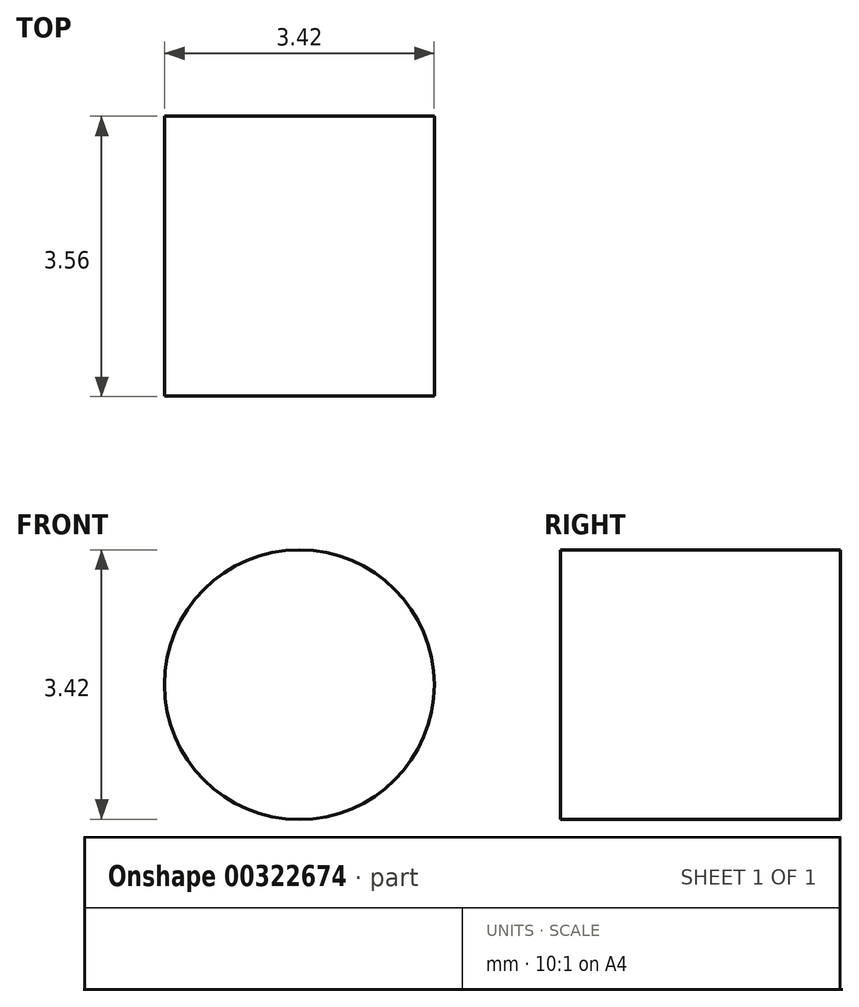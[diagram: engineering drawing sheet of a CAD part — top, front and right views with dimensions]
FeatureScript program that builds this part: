
annotation { "Feature Type Name" : "Feature", "Feature Type Description" : "" }
export const myFeature = defineFeature(function(context is Context, id is Id, definition is map)
    precondition{}
    {
        {
            var Q0;
            Q0=qCreatedBy(makeId("Front.planeOp"),FACE);
            var sketch = newSketch(context, id + "F0", { "sketchPlane" : qUnion([Q0])});
            skCircle(sketch, "E0", {"center": v(0, 0) * mm, "radius": 1.71 * mm});
            skSolve(sketch);
        }
        {
            var Q0;
            Q0 = qSketchRegion(id + "F0", true);
            extrude(context, id + "F1", {"entities" : qUnion([Q0]), "depth" : 3.56 * mm});
        }
    });
